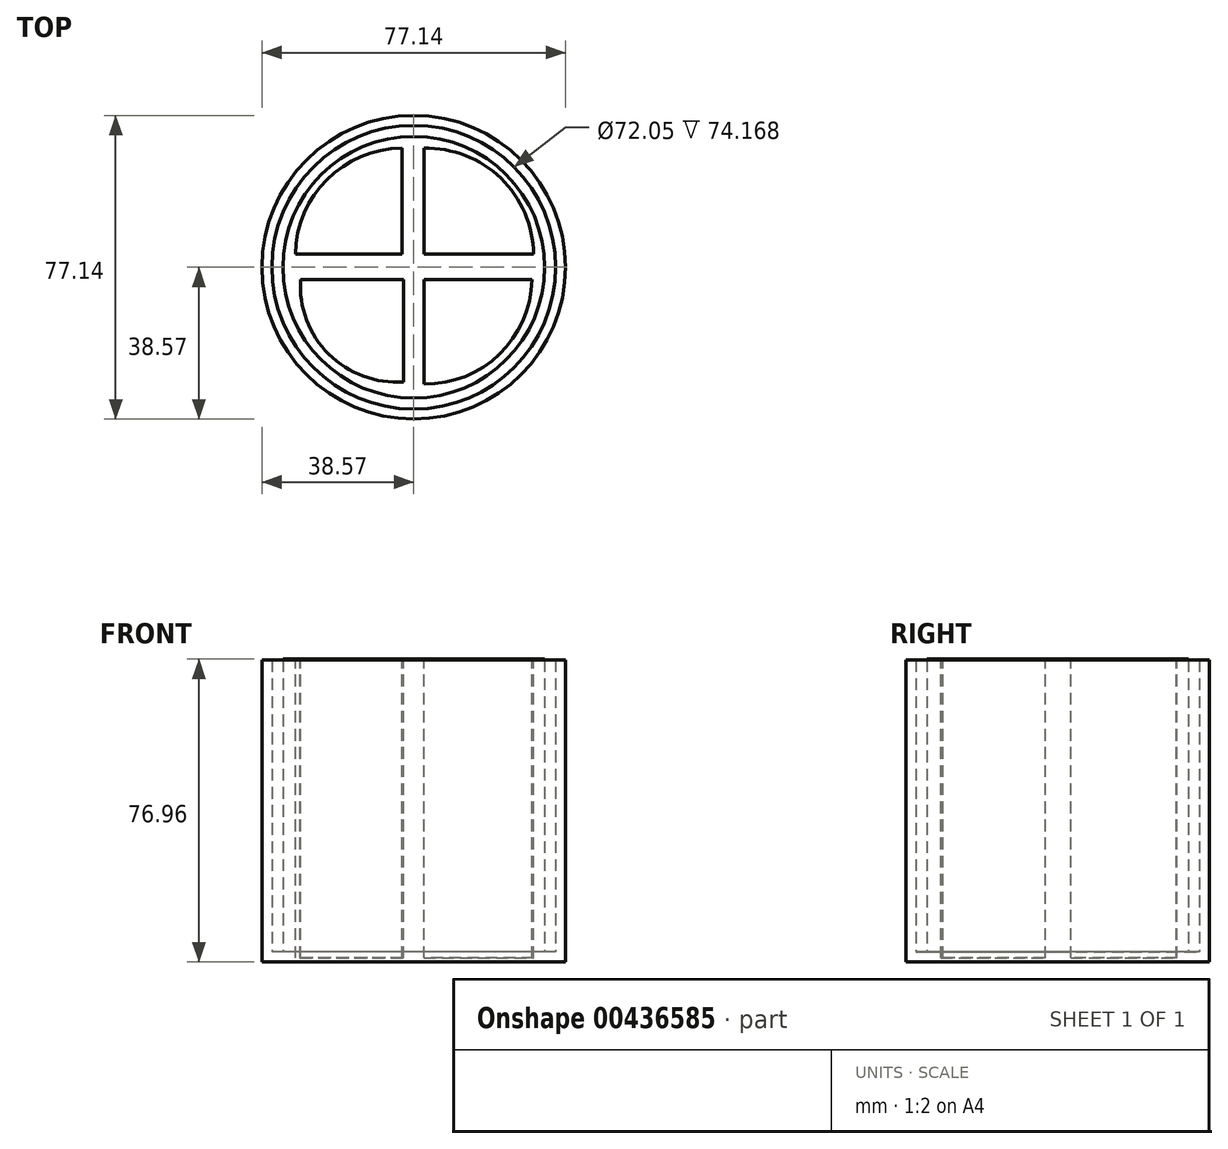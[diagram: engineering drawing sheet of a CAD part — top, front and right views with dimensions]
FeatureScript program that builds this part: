
annotation { "Feature Type Name" : "Feature", "Feature Type Description" : "" }
export const myFeature = defineFeature(function(context is Context, id is Id, definition is map)
    precondition{}
    {
        {
            var Q0;
            Q0=qCreatedBy(makeId("Top.planeOp"),FACE);
            var sketch = newSketch(context, id + "F0", { "sketchPlane" : qUnion([Q0])});
            skCircle(sketch, "E0", {"center": v(0, 0) * mm, "radius": 38.57 * mm});
            skSolve(sketch);
        }
        {
            var Q0;
            Q0 = qSketchRegion(id + "F0", true);
            extrude(context, id + "F1", {"entities" : qUnion([Q0]), "depth" : 76.7 * mm});
        }
        {
            var Q0;
            Q0=makeQuery(id+"F1.opExtrude","CAP_FACE",FACE,{"disambiguationData":[OSD([sQuery(id+"F0.wireOp",EDGE,"E0")])],"isStart":false});
            shell(context, id + "F2", {"entities" : qUnion([Q0]), "thickness" : 2.54 * mm});
        }
        {
            var Q0;
            {var subQ0=sQuery(id+"F0.wireOp",EDGE,"E0");Q0=makeQuery(id+"F2.opShell","OFFSET_FACE",FACE,{"disambiguationData":[OSD([subQ0]),TDD([makeQuery(id+"F1.opExtrude","CAP_FACE",FACE,{"disambiguationData":[OSD([subQ0])],"isStart":true})])]});}
            var sketch = newSketch(context, id + "F3", { "sketchPlane" : qUnion([Q0])});
            skCircle(sketch, "E1", {"center": v(0, 0) * mm, "radius": 33.24 * mm});
            skSolve(sketch);
        }
        {
            var Q0;
            Q0 = qSketchRegion(id + "F3", true);
            extrude(context, id + "F4", {"entities" : qUnion([Q0]), "operationType" : NewBodyOperationType.ADD, "depth" : 74.42 * mm});
        }
        {
            var Q0;
            Q0=makeQuery(id+"F4.opExtrude","CAP_FACE",FACE,{"disambiguationData":[OSD([sQuery(id+"F3.wireOp",EDGE,"E1")])],"isStart":false});
            var sketch = newSketch(context, id + "F5", { "sketchPlane" : qUnion([Q0])});
            skLineSegment(sketch, "E2", {"start": v(0, 33.24) * mm, "end": v(0, -33.24) * mm});
            skLineSegment(sketch, "E3", {"start": v(-33.24, 0) * mm, "end": v(33.24, 0) * mm});
            skLineSegment(sketch, "E4", {"start": v(2.58, 30.23) * mm, "end": v(2.58, 3.32) * mm});
            skLineSegment(sketch, "E5", {"start": v(2.58, 3.32) * mm, "end": v(30.42, 3.32) * mm});
            skLineSegment(sketch, "E6", {"start": v(2.58, -3.13) * mm, "end": v(2.58, -29.68) * mm});
            skLineSegment(sketch, "E7", {"start": v(2.58, -3.13) * mm, "end": v(30.05, -3.13) * mm});
            skLineSegment(sketch, "E8", {"start": v(-2.95, 30.23) * mm, "end": v(-2.95, 3.32) * mm});
            skLineSegment(sketch, "E9", {"start": v(-2.95, 3.32) * mm, "end": v(-30.05, 3.32) * mm});
            skLineSegment(sketch, "E10", {"start": v(-2.58, -3.13) * mm, "end": v(-2.58, -29.13) * mm});
            skLineSegment(sketch, "E11", {"start": v(-2.58, -3.13) * mm, "end": v(-28.76, -3.13) * mm});
            skArc(sketch, "E12", {"start": v(30.42, 3.32) * mm, "mid": v(22.14, 22.61) * mm, "end": v(2.58, 30.23) * mm});
            skArc(sketch, "E13", {"start": v(2.58, -29.68) * mm, "mid": v(21.8, -22.08) * mm, "end": v(30.05, -3.13) * mm});
            skArc(sketch, "E14", {"start": v(-2.95, 30.23) * mm, "mid": v(-22.01, 22.33) * mm, "end": v(-30.05, 3.32) * mm});
            skArc(sketch, "E15", {"start": v(-28.76, -3.13) * mm, "mid": v(-21.58, -22.08) * mm, "end": v(-2.58, -29.13) * mm});
            skSolve(sketch);
        }
        {
            var Q0;
            Q0 = qSketchRegion(id + "F5", true);
            extrude(context, id + "F6", {"entities" : qUnion([Q0]), "operationType" : NewBodyOperationType.REMOVE, "oppositeDirection" : true, "depth" : 75.95 * mm});
        }
    });
